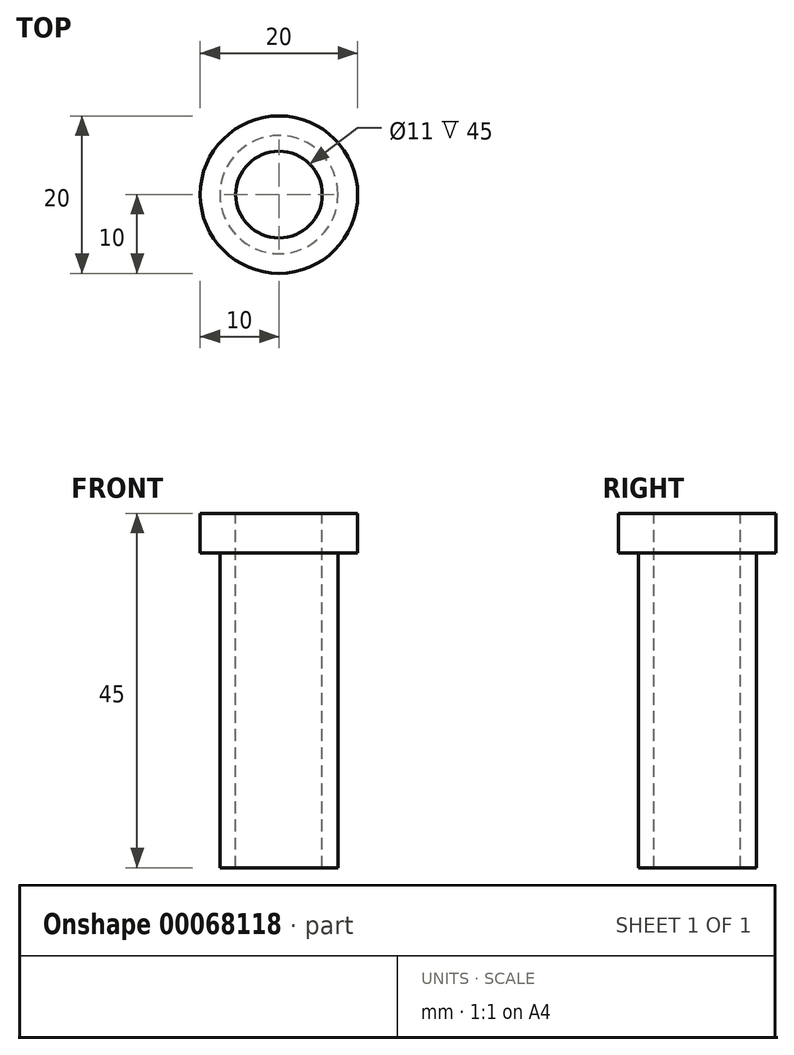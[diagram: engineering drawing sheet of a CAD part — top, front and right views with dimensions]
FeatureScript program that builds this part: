
annotation { "Feature Type Name" : "Feature", "Feature Type Description" : "" }
export const myFeature = defineFeature(function(context is Context, id is Id, definition is map)
    precondition{}
    {
        {
            var Q0;
            Q0=qCreatedBy(makeId("Front.planeOp"),FACE);
            var sketch = newSketch(context, id + "F0", { "sketchPlane" : qUnion([Q0])});
            skLineSegment(sketch, "E0", {"start": v(-5.5, -45) * mm, "end": v(-7.5, -45) * mm});
            skLineSegment(sketch, "E1", {"start": v(-7.5, -45) * mm, "end": v(-7.5, -5) * mm});
            skLineSegment(sketch, "E2", {"start": v(-7.5, -5) * mm, "end": v(-10, -5) * mm});
            skLineSegment(sketch, "E3", {"start": v(-10, -5) * mm, "end": v(-10, 0) * mm});
            skLineSegment(sketch, "E4", {"start": v(-10, 0) * mm, "end": v(-5.5, 0) * mm});
            skLineSegment(sketch, "E5", {"start": v(-5.5, 0) * mm, "end": v(-5.5, -45) * mm});
            skLineSegment(sketch, "E6", {"start": v(0, 0) * mm, "end": v(0, -44.62) * mm});
            skSolve(sketch);
        }
        {
            var Q0;
            Q0=makeQuery(id+"F0.imprint","IMPRINT",FACE,{"disambiguationData":[TD([[makeQuery(id+"F0.imprint","IMPRINT",EDGE,{"derivedFrom":sQuery(id+"F0.wireOp",EDGE,"E0")}),-1.0]])]});
            var Q1;
            Q1=sQuery(id+"F0.wireOp",EDGE,"E6");
            revolve(context, id + "F1", {"entities" : qUnion([Q0]), "axis" : qUnion([Q1]), "revolveType" : RevolveType.FULL});
        }
    });
